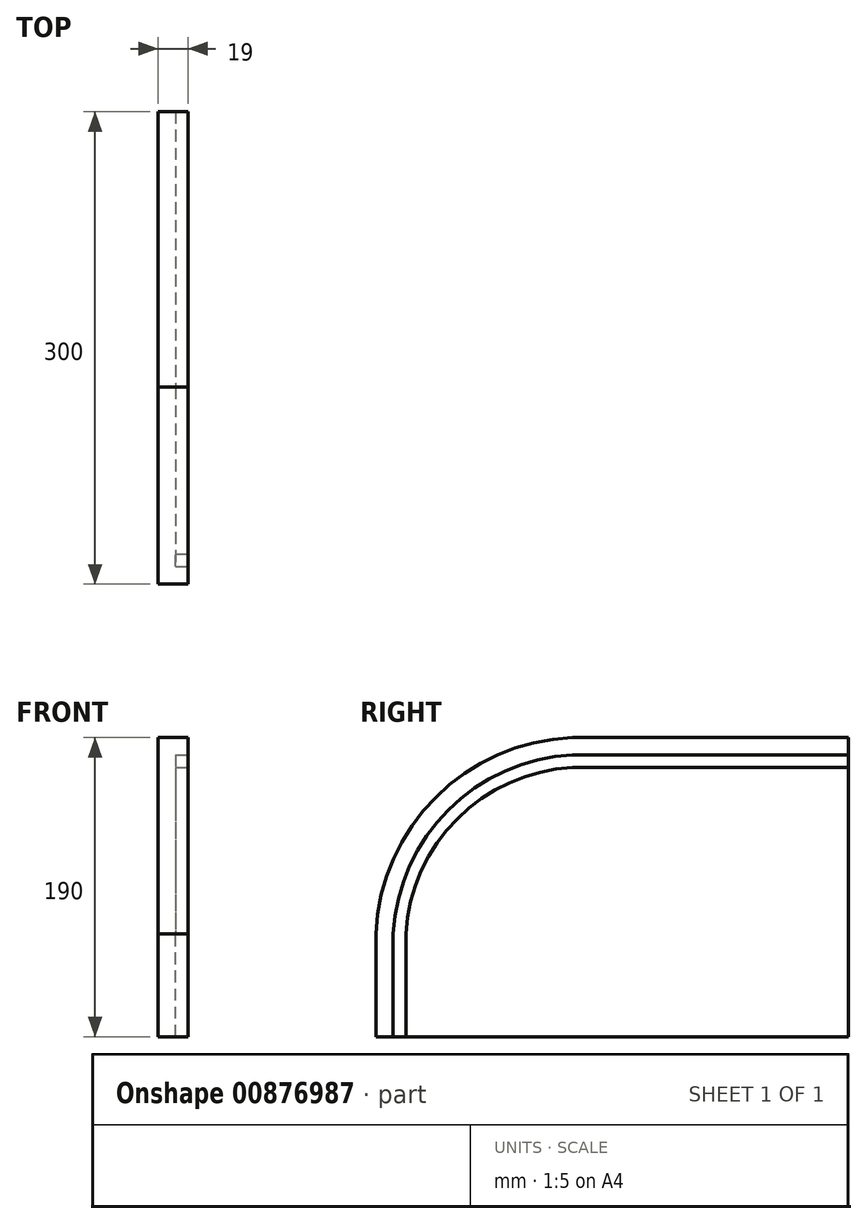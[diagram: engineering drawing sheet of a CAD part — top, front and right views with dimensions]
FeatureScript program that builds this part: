
annotation { "Feature Type Name" : "Feature", "Feature Type Description" : "" }
export const myFeature = defineFeature(function(context is Context, id is Id, definition is map)
    precondition{}
    {
        {
            var Q0;
            Q0=qCreatedBy(makeId("Right.planeOp"),FACE);
            var sketch = newSketch(context, id + "F0", { "sketchPlane" : qUnion([Q0]), "disableImprinting" : false});
            skLineSegment(sketch, "E0.bottom", {"start": v(-25, 95) * mm, "end": v(150, 95) * mm});
            skLineSegment(sketch, "E0.top", {"start": v(-150, -95) * mm, "end": v(150, -95) * mm});
            skLineSegment(sketch, "E0.left", {"start": v(-150, -29.82) * mm, "end": v(-150, -95) * mm});
            skLineSegment(sketch, "E0.right", {"start": v(150, 95) * mm, "end": v(150, -95) * mm});
            skPoint(sketch, "E0.middle", {"position": v(0, 0) * mm});
            skPoint(sketch, "E1", {"position": v(-150, -40) * mm});
            skPoint(sketch, "E2", {"position": v(-25, 95) * mm});
            skArc(sketch, "E3", {"start": v(-25, 95) * mm, "mid": v(-115.49, 53.42) * mm, "end": v(-150, -40) * mm});
            skPoint(sketch, "E4.orphan", {"position": v(-150, 95) * mm});
            skSolve(sketch);
        }
        {
            var Q0;
            {var subQ5=sQuery(id+"F0.wireOp",EDGE,"E0.bottom");Q0=makeQuery(id+"F0.imprint","IMPRINT",FACE,{"disambiguationData":[TD([[makeQuery(id+"F0.imprint","IMPRINT",EDGE,{"derivedFrom":subQ5}),-1.0]])]});}
            extrude(context, id + "F1", {"entities" : qUnion([Q0]), "depth" : 19 * mm, "offsetDistance" : 25 * mm});
        }
        {
            var Q0;
            Q0=makeQuery(id+"F1.opExtrude","CAP_FACE",FACE,{"disambiguationData":[OSD([sQuery(id+"F0.wireOp",EDGE,"E0.bottom"),sQuery(id+"F0.wireOp",EDGE,"E0.top"),sQuery(id+"F0.wireOp",EDGE,"E0.left"),sQuery(id+"F0.wireOp",EDGE,"E0.right"),sQuery(id+"F0.wireOp",EDGE,"E3")])],"isStart":false});
            var sketch = newSketch(context, id + "F2", { "sketchPlane" : qUnion([Q0]), "disableImprinting" : false});
            skPoint(sketch, "E5", {"position": v(150, 84) * mm});
            skPoint(sketch, "E6", {"position": v(150, 76) * mm});
            skLineSegment(sketch, "E7", {"start": v(150, 84) * mm, "end": v(-25, 84) * mm});
            skLineSegment(sketch, "E8", {"start": v(150, 76) * mm, "end": v(-25, 76) * mm});
            skPoint(sketch, "E9", {"position": v(-139, -95) * mm});
            skPoint(sketch, "E10", {"position": v(-131, -95) * mm});
            skLineSegment(sketch, "E11", {"start": v(-139, -95) * mm, "end": v(-139, -29.82) * mm});
            skLineSegment(sketch, "E12", {"start": v(-131, -95) * mm, "end": v(-131, -29.82) * mm});
            skArc(sketch, "E13", {"start": v(-25, 76) * mm, "mid": v(-98.29, 43.42) * mm, "end": v(-131, -29.82) * mm});
            skArc(sketch, "E14", {"start": v(-25, 84) * mm, "mid": v(-103.94, 49.06) * mm, "end": v(-139, -29.82) * mm});
            skSolve(sketch);
        }
        {
            var Q0;
            {var subQ1=sQuery(id+"F2.wireOp",EDGE,"E7");Q0=makeQuery(id+"F2.imprint","IMPRINT",FACE,{"disambiguationData":[TD([[makeQuery(id+"F2.imprint","IMPRINT",EDGE,{"derivedFrom":subQ1}),1.0]])]});}
            extrude(context, id + "F3", {"entities" : qUnion([Q0]), "operationType" : NewBodyOperationType.REMOVE, "oppositeDirection" : true, "depth" : 8 * mm, "offsetDistance" : 25 * mm});
        }
    });
